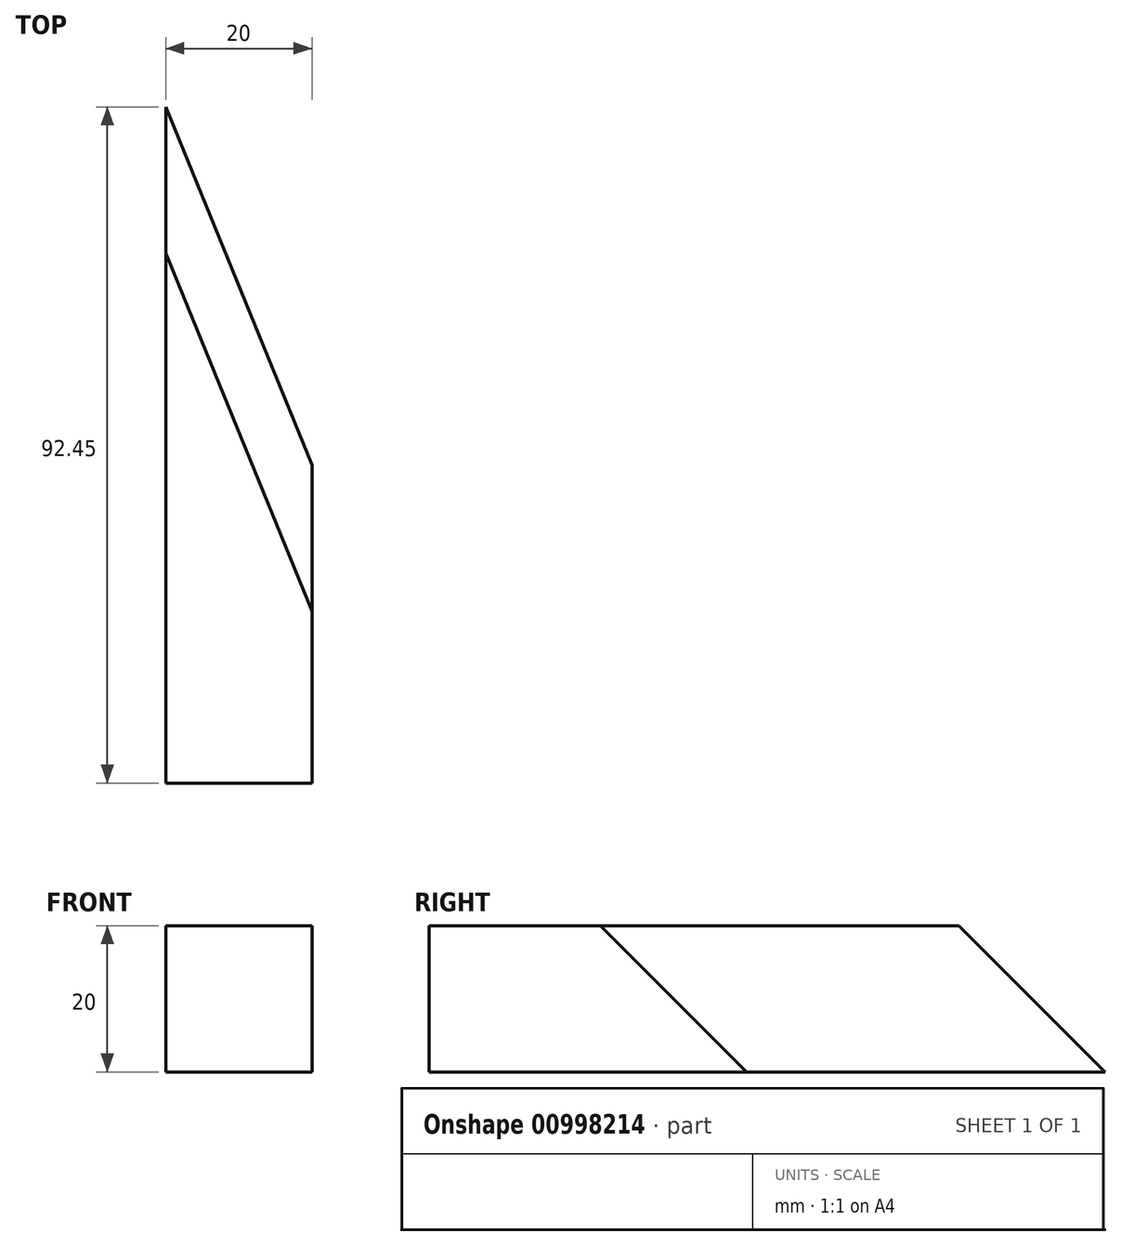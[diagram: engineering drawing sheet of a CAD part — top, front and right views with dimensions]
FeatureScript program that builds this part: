
annotation { "Feature Type Name" : "Feature", "Feature Type Description" : "" }
export const myFeature = defineFeature(function(context is Context, id is Id, definition is map)
    precondition{}
    {
        {
            var Q0;
            Q0=qCreatedBy(makeId("Front.planeOp"),FACE);
            var sketch = newSketch(context, id + "F0", { "sketchPlane" : qUnion([Q0])});
            skLineSegment(sketch, "E0.bottom", {"start": v(10, 10) * mm, "end": v(-10, 10) * mm});
            skLineSegment(sketch, "E0.top", {"start": v(10, -10) * mm, "end": v(-10, -10) * mm});
            skLineSegment(sketch, "E0.left", {"start": v(10, 10) * mm, "end": v(10, -10) * mm});
            skLineSegment(sketch, "E0.right", {"start": v(-10, 10) * mm, "end": v(-10, -10) * mm});
            skPoint(sketch, "E0.middle", {"position": v(0, 0) * mm});
            skSolve(sketch);
        }
        {
            var Q0;
            Q0 = qSketchRegion(id + "F0", true);
            extrude(context, id + "F1", {"entities" : qUnion([Q0]), "depth" : 100 * mm, "offsetDistance" : 25 * mm});
        }
        {
            var Q0;
            Q0=makeQuery(id+"F1.opExtrude","CAP_EDGE",EDGE,{"disambiguationData":[OSD([sQuery(id+"F0.wireOp",EDGE,"E0.bottom")])],"isStart":true});
            var Q1;
            Q1=qCreatedBy(makeId("Top.planeOp"),FACE);
            cPlane(context, id + "F2", {"entities" : qUnion([Q0, Q1]), "cplaneType" : CPlaneType.LINE_ANGLE, "offset" : 25 * mm, "angle" : 45 * degree, "width" : 150 * mm, "height" : 150 * mm});
        }
        {
            var Q0;
            Q0=qCreatedBy(id+"F2.planeOp",FACE);
            var sketch = newSketch(context, id + "F3", { "sketchPlane" : qUnion([Q0])});
            skLineSegment(sketch, "E1", {"start": v(0, -7.68) * mm, "end": v(0, 10.93) * mm, "construction": true});
            skSolve(sketch);
        }
        {
            var Q0;
            Q0=sQuery(id+"F3.wireOp",EDGE,"E1");
            var Q1;
            Q1=qCreatedBy(id+"F2.planeOp",FACE);
            cPlane(context, id + "F4", {"entities" : qUnion([Q0, Q1]), "cplaneType" : CPlaneType.LINE_ANGLE, "offset" : 25 * mm, "angle" : 60 * degree, "oppositeDirection" : true, "width" : 150 * mm, "height" : 150 * mm});
        }
        {
            var Q0;
            Q0=qCreatedBy(id+"F4.planeOp",FACE);
            var sketch = newSketch(context, id + "F5", { "sketchPlane" : qUnion([Q0])});
            skLineSegment(sketch, "E2.bottom", {"start": v(-302.04, -182.3) * mm, "end": v(225.36, -182.3) * mm});
            skLineSegment(sketch, "E2.top", {"start": v(-302.04, 304.47) * mm, "end": v(225.36, 304.47) * mm});
            skLineSegment(sketch, "E2.left", {"start": v(-302.04, -182.3) * mm, "end": v(-302.04, 304.47) * mm});
            skLineSegment(sketch, "E2.right", {"start": v(225.36, -182.3) * mm, "end": v(225.36, 304.47) * mm});
            skSolve(sketch);
        }
        {
            var Q0;
            Q0 = qSketchRegion(id + "F5", true);
            extrude(context, id + "F6", {"entities" : qUnion([Q0]), "operationType" : NewBodyOperationType.REMOVE, "oppositeDirection" : true, "depth" : 18.4 * mm, "offsetDistance" : 25 * mm, "hasSecondDirection" : true, "secondDirectionBound" : SecondDirectionBoundingType.THROUGH_ALL, "secondDirectionOppositeDirection" : false, "secondDirectionDepth" : 25 * mm});
        }
        {
            var Q0;
            Q0=makeQuery(id+"F6.boolean.opBoolean","INTERSECT",EDGE,{"derivedFrom":[makeQuery(id+"F1.opExtrude","SWEPT_FACE",FACE,{"disambiguationData":[OSD([sQuery(id+"F0.wireOp",EDGE,"E0.right")])]}),makeQuery(id+"F6.opExtrude","CAP_FACE",FACE,{"disambiguationData":[OSD([sQuery(id+"F5.wireOp",EDGE,"E2.bottom"),sQuery(id+"F5.wireOp",EDGE,"E2.top"),sQuery(id+"F5.wireOp",EDGE,"E2.left"),sQuery(id+"F5.wireOp",EDGE,"E2.right")])],"isStart":false})]});
            cPlane(context, id + "F7", {"entities" : qUnion([Q0]), "cplaneType" : CPlaneType.MID_PLANE, "offset" : 25 * mm, "width" : 150 * mm, "height" : 150 * mm});
        }
        {
            var Q0;
            Q0=makeQuery(id+"F6.boolean.opBoolean","INTERSECT",EDGE,{"derivedFrom":[makeQuery(id+"F1.opExtrude","SWEPT_FACE",FACE,{"disambiguationData":[OSD([sQuery(id+"F0.wireOp",EDGE,"E0.bottom")])]}),makeQuery(id+"F6.opExtrude","CAP_FACE",FACE,{"disambiguationData":[OSD([sQuery(id+"F5.wireOp",EDGE,"E2.bottom"),sQuery(id+"F5.wireOp",EDGE,"E2.top"),sQuery(id+"F5.wireOp",EDGE,"E2.left"),sQuery(id+"F5.wireOp",EDGE,"E2.right")])],"isStart":false})]});
            cPlane(context, id + "F8", {"entities" : qUnion([Q0]), "cplaneType" : CPlaneType.MID_PLANE, "offset" : 25 * mm, "width" : 150 * mm, "height" : 150 * mm});
        }
    });
